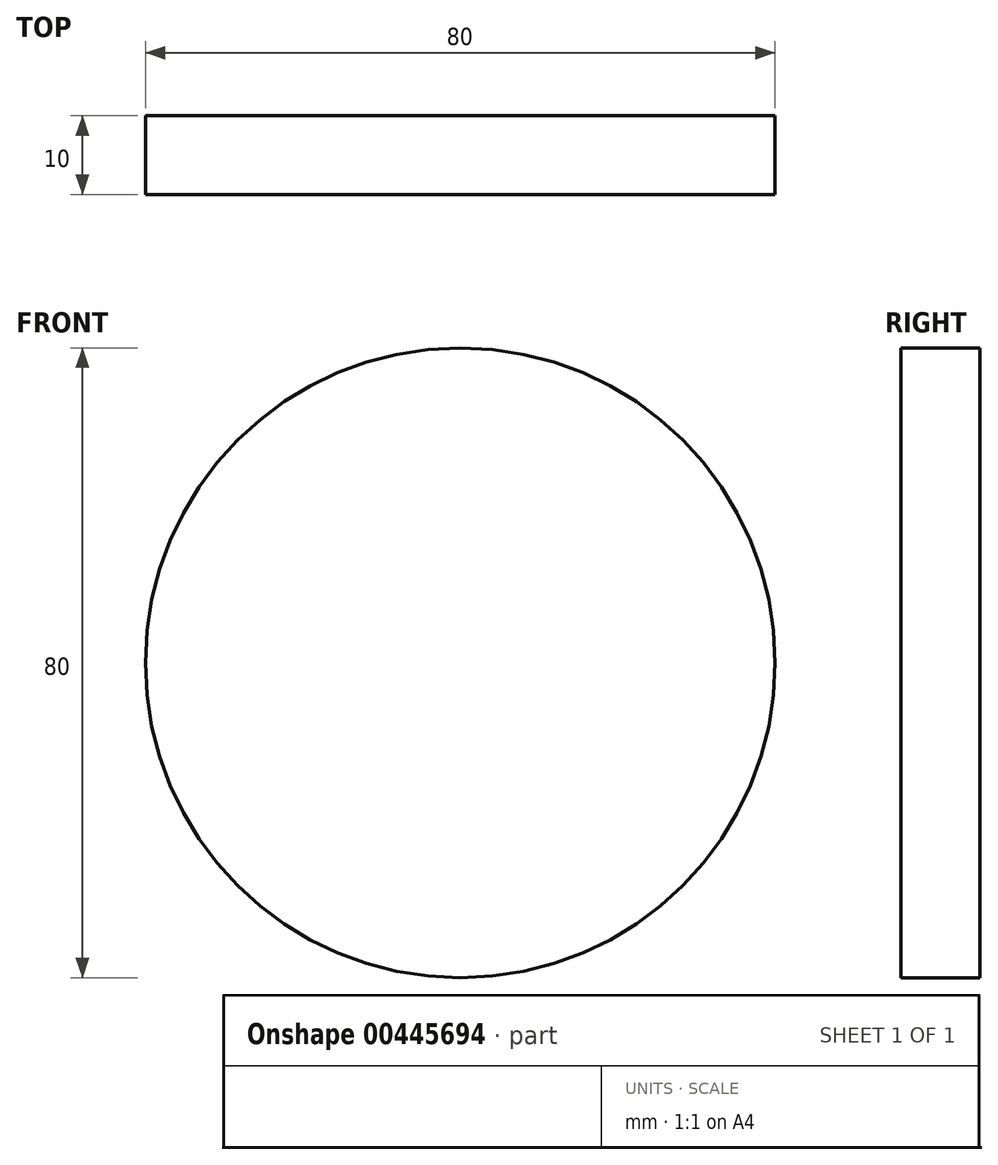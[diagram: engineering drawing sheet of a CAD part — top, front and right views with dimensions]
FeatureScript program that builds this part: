
annotation { "Feature Type Name" : "Feature", "Feature Type Description" : "" }
export const myFeature = defineFeature(function(context is Context, id is Id, definition is map)
    precondition{}
    {
        {
            var Q0;
            Q0=qCreatedBy(makeId("Front.planeOp"),FACE);
            var sketch = newSketch(context, id + "F0", { "sketchPlane" : qUnion([Q0])});
            skCircle(sketch, "E0", {"center": v(0, 0) * mm, "radius": 40 * mm});
            skSolve(sketch);
        }
        {
            var Q0;
            Q0=makeQuery(id+"F0.imprint","IMPRINT",FACE,{"disambiguationData":[TD([[makeQuery(id+"F0.imprint","IMPRINT",EDGE,{"derivedFrom":sQuery(id+"F0.wireOp",EDGE,"E0")}),1.0]])]});
            extrude(context, id + "F1", {"entities" : qUnion([Q0]), "depth" : 10 * mm});
        }
        {
            var Q0;
            Q0=qCreatedBy(makeId("Front.planeOp"),FACE);
            var sketch = newSketch(context, id + "F2", { "sketchPlane" : qUnion([Q0])});
            skCircle(sketch, "E1", {"center": v(0, 0) * mm, "radius": 5 * mm});
            skSolve(sketch);
        }
        {
            var Q0;
            Q0=sQuery(id+"F2.wireOp",EDGE,"E1");
            extrude(context, id + "F3", {"bodyType" : ToolBodyType.SURFACE, "surfaceEntities" : qUnion([Q0]), "depth" : 100 * mm});
        }
    });
